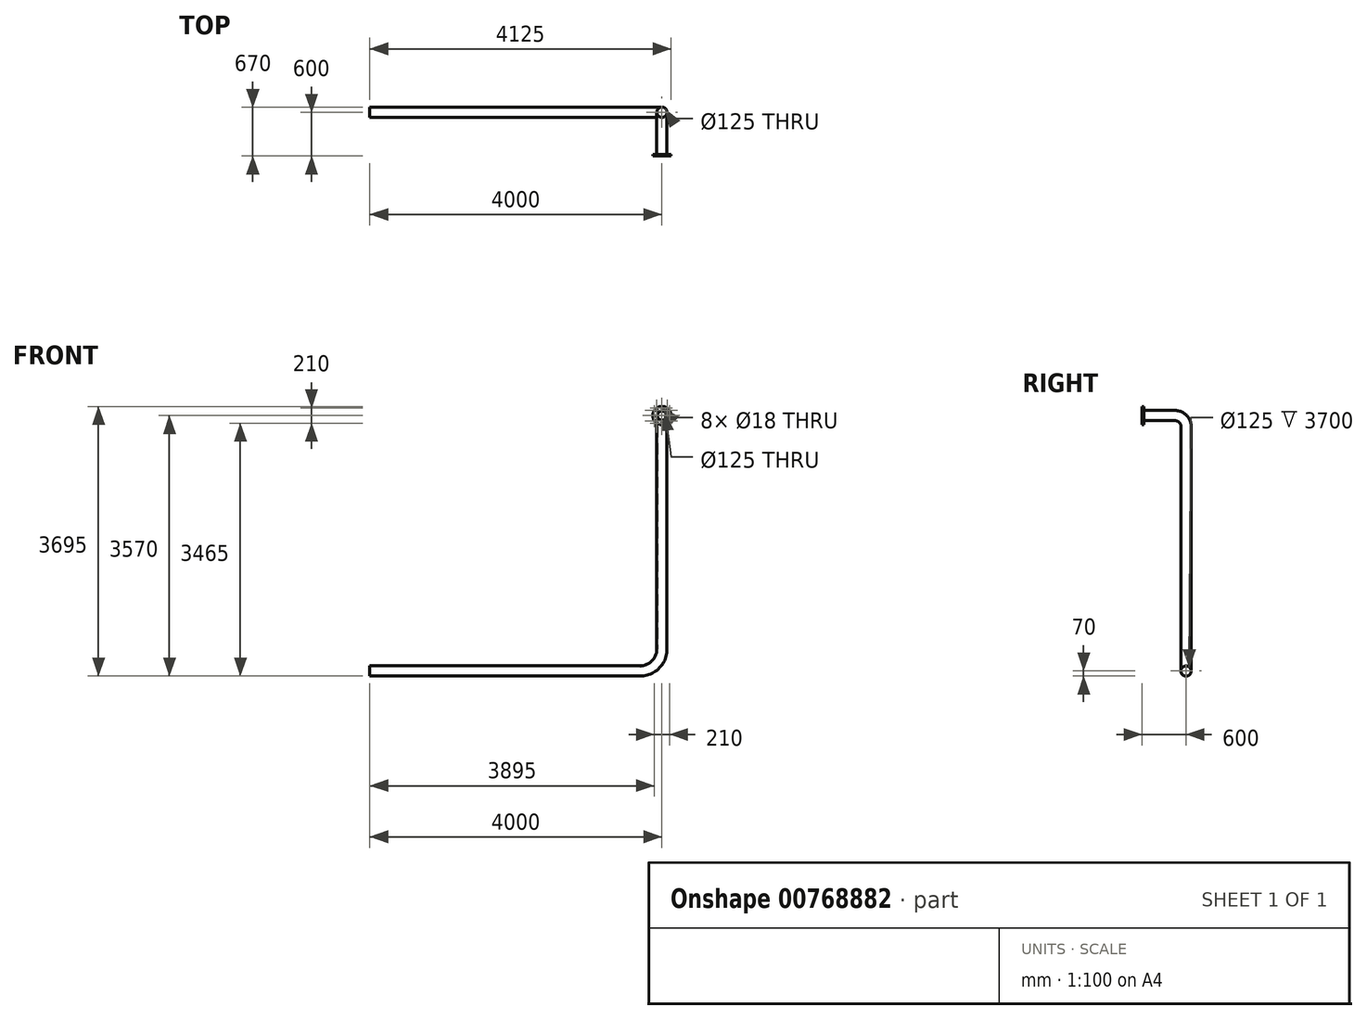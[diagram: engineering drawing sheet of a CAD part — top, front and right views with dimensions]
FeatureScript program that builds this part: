
annotation { "Feature Type Name" : "Feature", "Feature Type Description" : "" }
export const myFeature = defineFeature(function(context is Context, id is Id, definition is map)
    precondition{}
    {
        {
            var Q0;
            Q0=qCreatedBy(makeId("Front.planeOp"),FACE);
            var sketch = newSketch(context, id + "F0", { "sketchPlane" : qUnion([Q0])});
            skCircle(sketch, "E0", {"center": v(0, 0) * mm, "radius": 62.5 * mm});
            skCircle(sketch, "E1", {"center": v(0, 0) * mm, "radius": 125 * mm});
            skCircle(sketch, "E2", {"center": v(0, 0) * mm, "radius": 70 * mm});
            skCircle(sketch, "E3", {"center": v(0, 105) * mm, "radius": 9 * mm});
            skCircle(sketch, "E4.1.0", {"center": v(-74.25, 74.25) * mm, "radius": 9 * mm});
            skCircle(sketch, "E4.2.0", {"center": v(-105, 0) * mm, "radius": 9 * mm});
            skCircle(sketch, "E4.3.0", {"center": v(-74.25, -74.25) * mm, "radius": 9 * mm});
            skCircle(sketch, "E4.4.0", {"center": v(0, -105) * mm, "radius": 9 * mm});
            skCircle(sketch, "E4.5.0", {"center": v(74.25, -74.25) * mm, "radius": 9 * mm});
            skCircle(sketch, "E4.6.0", {"center": v(105, 0) * mm, "radius": 9 * mm});
            skCircle(sketch, "E4.7.0", {"center": v(74.25, 74.25) * mm, "radius": 9 * mm});
            skSolve(sketch);
        }
        {
            var Q0;
            Q0=qCreatedBy(makeId("Right.planeOp"),FACE);
            var sketch = newSketch(context, id + "F1", { "sketchPlane" : qUnion([Q0])});
            skLineSegment(sketch, "E5", {"start": v(0, 0) * mm, "end": v(450, 0) * mm});
            skLineSegment(sketch, "E6", {"start": v(600, -150) * mm, "end": v(600, -3500) * mm});
            skPoint(sketch, "E7.visualSharp", {"position": v(600, 0) * mm});
            skArc(sketch, "E7.filletArc", {"start": v(600, -150) * mm, "mid": v(556.07, -43.93) * mm, "end": v(450, 0) * mm});
            skSolve(sketch);
        }
        {
            var Q0;
            Q0=qCreatedBy(makeId("Front.planeOp"),FACE);
            cPlane(context, id + "F2", {"entities" : qUnion([Q0]), "cplaneType" : CPlaneType.OFFSET, "offset" : 600 * mm, "oppositeDirection" : true, "width" : 150 * mm, "height" : 150 * mm});
        }
        {
            var Q0;
            Q0=qCreatedBy(id+"F2.planeOp",FACE);
            var sketch = newSketch(context, id + "F3", { "sketchPlane" : qUnion([Q0])});
            skLineSegment(sketch, "E8.0", {"start": v(0, -150) * mm, "end": v(0, -3200) * mm});
            skLineSegment(sketch, "E9", {"start": v(-300, -3500) * mm, "end": v(-4000, -3500) * mm});
            skPoint(sketch, "E10.visualSharp", {"position": v(0, -3500) * mm});
            skArc(sketch, "E10.filletArc", {"start": v(-300, -3500) * mm, "mid": v(-87.87, -3412.13) * mm, "end": v(0, -3200) * mm});
            skSolve(sketch);
        }
        {
            var Q0;
            Q0=makeQuery(id+"F0.imprint","IMPRINT",FACE,{"disambiguationData":[TD([[makeQuery(id+"F0.imprint","IMPRINT",EDGE,{"derivedFrom":sQuery(id+"F0.wireOp",EDGE,"E0")}),-1.0]])]});
            var Q1;
            Q1=sQuery(id+"F1.wireOp",EDGE,"E5");
            var Q2;
            Q2=sQuery(id+"F1.wireOp",EDGE,"E7.filletArc");
            var Q3;
            Q3=sQuery(id+"F3.wireOp",EDGE,"E8.0");
            var Q4;
            Q4=sQuery(id+"F3.wireOp",EDGE,"E10.filletArc");
            var Q5;
            Q5=sQuery(id+"F3.wireOp",EDGE,"E9");
            sweep(context, id + "F4", {"profiles" : qUnion([Q0]), "path" : qUnion([Q1, Q2, Q3, Q4, Q5])});
        }
        {
            var Q0;
            Q0=makeQuery(id+"F0.imprint","IMPRINT",FACE,{"disambiguationData":[TD([[makeQuery(id+"F0.imprint","IMPRINT",EDGE,{"derivedFrom":sQuery(id+"F0.wireOp",EDGE,"E1")}),1.0]])]});
            extrude(context, id + "F5", {"entities" : qUnion([Q0]), "operationType" : NewBodyOperationType.ADD, "oppositeDirection" : true, "depth" : 20 * mm, "offsetDistance" : 25 * mm});
        }
    });
